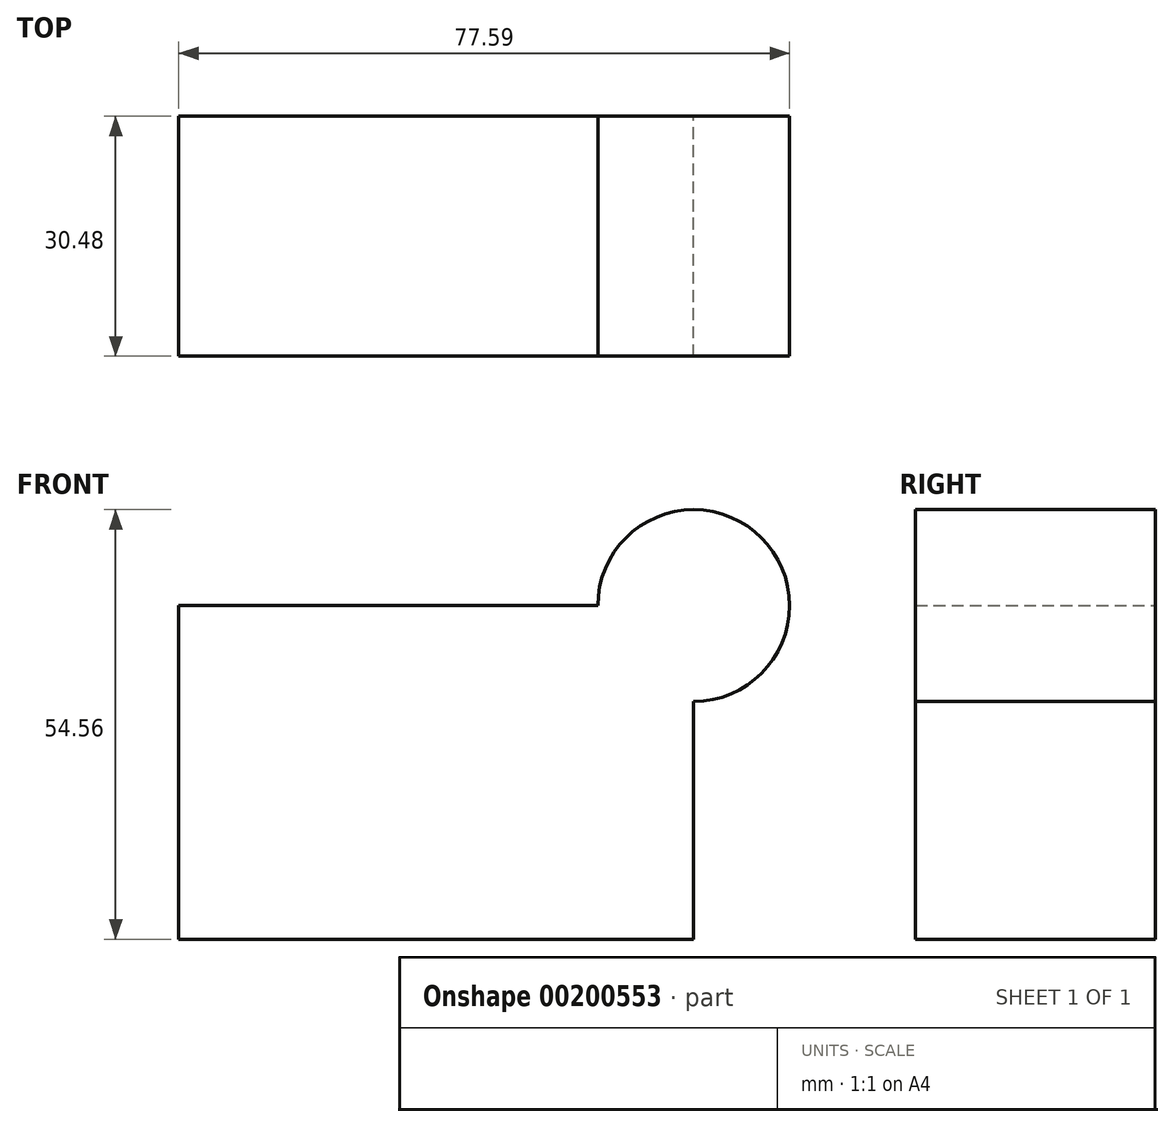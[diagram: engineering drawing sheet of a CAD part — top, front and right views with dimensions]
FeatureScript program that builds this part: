
annotation { "Feature Type Name" : "Feature", "Feature Type Description" : "" }
export const myFeature = defineFeature(function(context is Context, id is Id, definition is map)
    precondition{}
    {
        {
            var Q0;
            Q0=qCreatedBy(makeId("Front.planeOp"),FACE);
            var sketch = newSketch(context, id + "F0", { "sketchPlane" : qUnion([Q0])});
            skLineSegment(sketch, "E0.bottom", {"start": v(-52.26, 15.2) * mm, "end": v(13.15, 15.2) * mm});
            skLineSegment(sketch, "E0.top", {"start": v(-52.26, -27.18) * mm, "end": v(13.15, -27.18) * mm});
            skLineSegment(sketch, "E0.left", {"start": v(-52.26, 15.2) * mm, "end": v(-52.26, -27.18) * mm});
            skLineSegment(sketch, "E0.right", {"start": v(13.15, 15.2) * mm, "end": v(13.15, -27.18) * mm});
            skCircle(sketch, "E1", {"center": v(13.15, 15.2) * mm, "radius": 12.18 * mm});
            skSolve(sketch);
        }
        {
            var Q0;
            Q0 = qSketchRegion(id + "F0", true);
            extrude(context, id + "F1", {"entities" : qUnion([Q0]), "depth" : 30.48 * mm});
        }
    });
